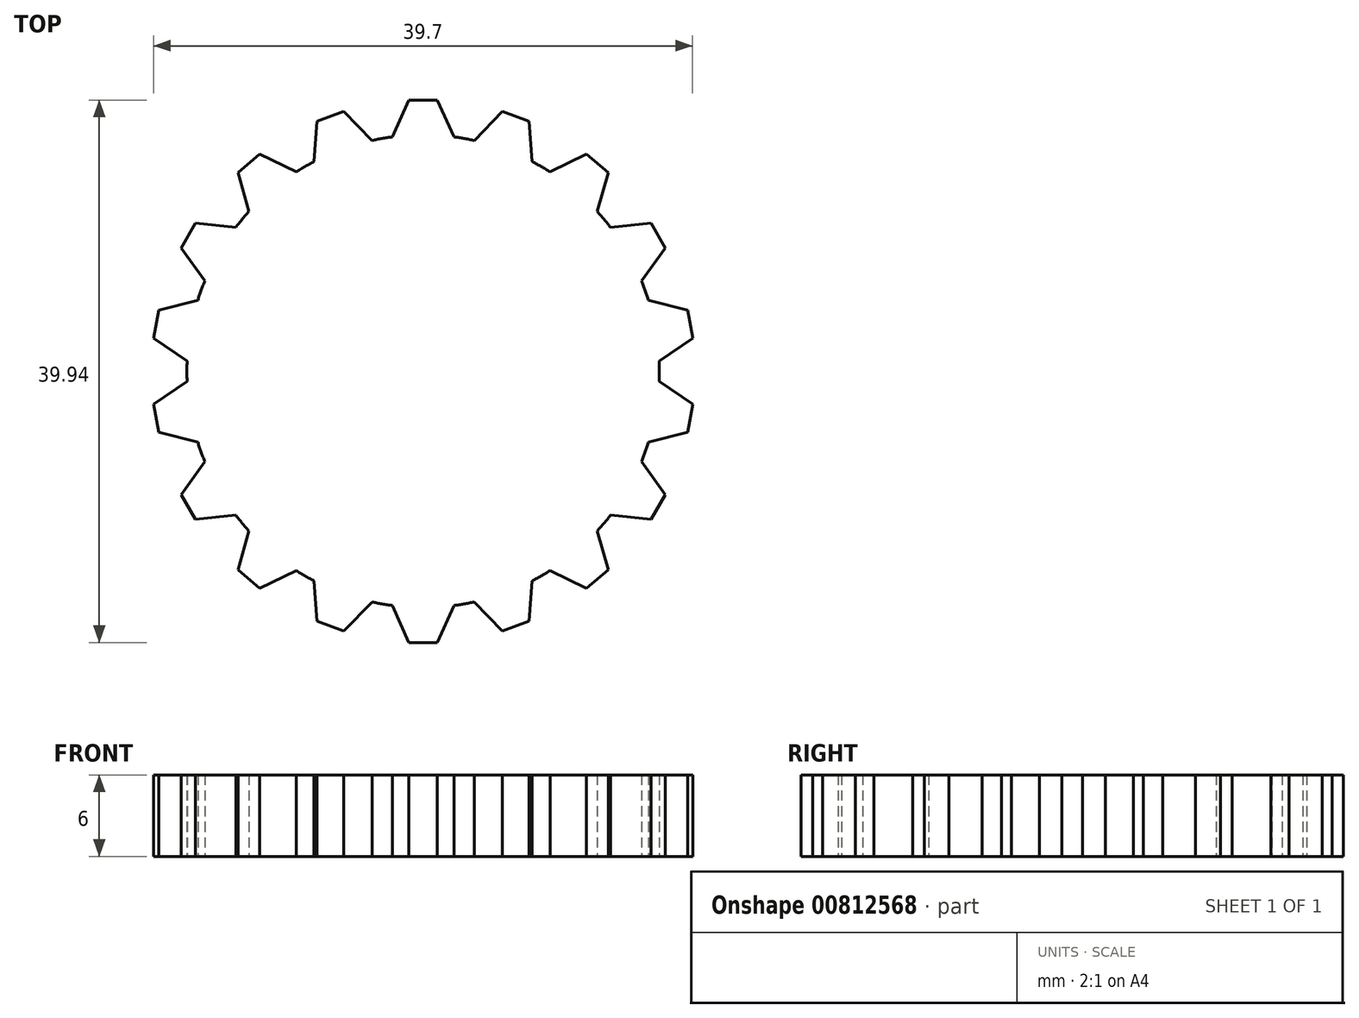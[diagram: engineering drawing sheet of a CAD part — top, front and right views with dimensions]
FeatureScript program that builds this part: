
annotation { "Feature Type Name" : "Feature", "Feature Type Description" : "" }
export const myFeature = defineFeature(function(context is Context, id is Id, definition is map)
    precondition{}
    {
        {
            var Q0;
            Q0=qCreatedBy(makeId("Top.planeOp"),FACE);
            var sketch = newSketch(context, id + "F0", { "sketchPlane" : qUnion([Q0])});
            skCircle(sketch, "E0", {"center": v(0, 0) * mm, "radius": 17.4 * mm, "construction": true});
            skCircle(sketch, "E1", {"center": v(0, 0) * mm, "radius": 20 * mm, "construction": true});
            skLineSegment(sketch, "E2", {"start": v(0, 0) * mm, "end": v(0, 27.02) * mm, "construction": true});
            skLineSegment(sketch, "E3", {"start": v(0, 0) * mm, "end": v(-2.84, 21.54) * mm, "construction": true});
            skLineSegment(sketch, "E4", {"start": v(0, 0) * mm, "end": v(-1.42, 27.06) * mm, "construction": true});
            skPoint(sketch, "E4.endSnap0", {"position": v(-1.42, 10.77) * mm});
            skLineSegment(sketch, "E5", {"start": v(-2.27, 17.25) * mm, "end": v(-1.05, 19.97) * mm});
            skLineSegment(sketch, "E6", {"start": v(-1.05, 19.97) * mm, "end": v(0, 19.97) * mm});
            skLineSegment(sketch, "E7.MirrorCS", {"start": v(2.27, 17.25) * mm, "end": v(1.05, 19.97) * mm});
            skLineSegment(sketch, "E8.MirrorCS", {"start": v(1.05, 19.97) * mm, "end": v(0, 19.97) * mm});
            skLineSegment(sketch, "E9", {"start": v(-2.27, 17.25) * mm, "end": v(2.27, 17.25) * mm});
            skSolve(sketch);
        }
        {
            var Q0;
            Q0=qCreatedBy(makeId("Top.planeOp"),FACE);
            var sketch = newSketch(context, id + "F1", { "sketchPlane" : qUnion([Q0])});
            skCircle(sketch, "E10", {"center": v(0, 0) * mm, "radius": 17.4 * mm});
            skSolve(sketch);
        }
        {
            var Q0;
            Q0=qSketchRegion(id+"F1",true);
            var Q1;
            Q1=qSketchRegion(id+"F0",true);
            extrude(context, id + "F2", {"entities" : qUnion([Q0, Q1]), "depth" : 6 * mm, "offsetDistance" : 25 * mm});
        }
        {
            var Q0;
            Q0=qCreatedBy(makeId("Front.planeOp"),FACE);
            var sketch = newSketch(context, id + "F3", { "sketchPlane" : qUnion([Q0])});
            skLineSegment(sketch, "E11", {"start": v(0, 0) * mm, "end": v(0, 3) * mm});
            skLineSegment(sketch, "E12", {"start": v(0, 3) * mm, "end": v(-14.4, 6) * mm});
            skLineSegment(sketch, "E13", {"start": v(-14.4, 6) * mm, "end": v(-17.4, 6) * mm});
            skLineSegment(sketch, "E14", {"start": v(-17.4, 6) * mm, "end": v(-20, 4.5) * mm});
            skLineSegment(sketch, "E15", {"start": v(-20, 4.5) * mm, "end": v(-20, 1.5) * mm});
            skLineSegment(sketch, "E16", {"start": v(-20, 1.5) * mm, "end": v(-17.4, 0) * mm});
            skLineSegment(sketch, "E17", {"start": v(-17.4, 0) * mm, "end": v(0, 0) * mm});
            skSolve(sketch);
        }
        {
            var Q0;
            Q0=makeQuery(id+"F2.opExtrude","SWEPT_BODY",BODY,{"disambiguationData":[OSD([sQuery(id+"F0.wireOp",EDGE,"E5"),sQuery(id+"F0.wireOp",EDGE,"E6"),sQuery(id+"F0.wireOp",EDGE,"E7.MirrorCS"),sQuery(id+"F0.wireOp",EDGE,"E8.MirrorCS"),sQuery(id+"F0.wireOp",EDGE,"E9")])]});
            var Q1;
            Q1=sQuery(id+"F3.wireOp",EDGE,"E11");
            circularPattern(context, id + "F4", {"operationType" : NewBodyOperationType.ADD, "entities" : qUnion([Q0]), "axis" : qUnion([Q1]), "angle" : 360 * degree, "instanceCount" : 18, "equalSpace" : true});
        }
    });
